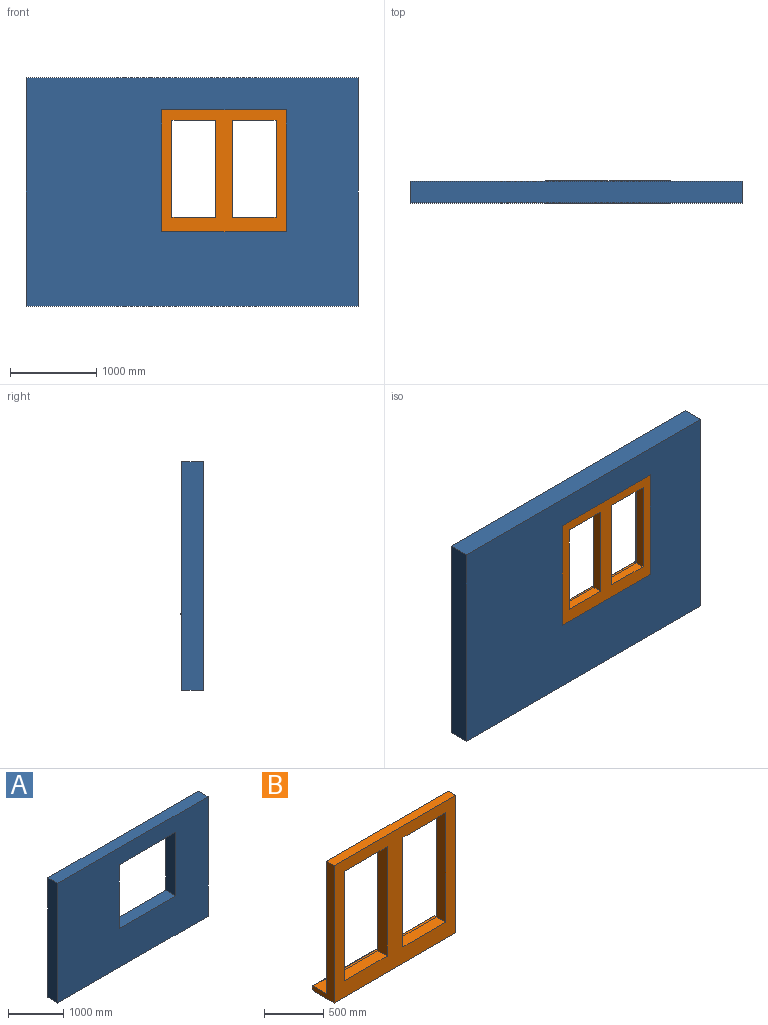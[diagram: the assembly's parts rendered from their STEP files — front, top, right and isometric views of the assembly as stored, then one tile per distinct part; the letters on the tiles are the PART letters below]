
ASSEMBLY  parts=2 mates=1
PART A: 10 faces, bbox 3860x250x2655 mm
  f0: plane 3860x250mm, normal (0,0,1), area 965000mm2, adj f1,f3,f4,f5
  f1: plane 2655x250mm, normal (-1,0,0), area 663750mm2, adj f0,f2,f3,f5
  f2: plane 3860x250mm, normal (0,0,-1), area 965000mm2, adj f1,f3,f4,f5
  f3: plane 3860x2655mm, normal (0,-1,0), area 8193648.2mm2, adj f0,f1,f2,f4,f6,f7,f8,f9
  f4: plane 2655x250mm, normal (1,0,0), area 663750mm2, adj f0,f2,f3,f5
  f5: plane 3860x2655mm, normal (0,1,0), area 8193648.2mm2, adj f0,f1,f2,f4,f6,f7,f8,f9
  f6: plane 1417x250mm, normal (1,0,0), area 354250.3mm2, adj f3,f5,f7,f9
  f7: plane 1450x250mm, normal (0,0,-1), area 362500mm2, adj f3,f5,f6,f8
  f8: plane 1417x250mm, normal (-1,0,0), area 354250.3mm2, adj f3,f5,f7,f9
  f9: plane 1450x250mm, normal (0,0,1), area 362500mm2, adj f3,f5,f6,f8
PART B: 29 faces, bbox 1450x263x1417 mm
  f0: plane 1450x1417mm, normal (0,-1,0), area 901835.8mm2, adj f16,f17,f18,f19,f20,f21,f22,f23
  f1: plane 1450x12mm, normal (0,1,0), area 17401.8mm2, adj f24,f25,f26,f28
  f2: plane 671x20mm, normal (0,0,-1), area 13420mm2, adj f3,f5,f10,f12
  f3: plane 1288x20mm, normal (-1,0,0), area 25760mm2, adj f2,f4,f10,f12
  f4: plane 671x20mm, normal (0,0,1), area 13420mm2, adj f3,f5,f10,f12
  f5: plane 1288x20mm, normal (1,0,0), area 25760mm2, adj f2,f4,f10,f12
  f6: plane 1288x20mm, normal (-1,0,0), area 25760mm2, adj f7,f9,f11,f12
  f7: plane 671x20mm, normal (0,0,1), area 13420mm2, adj f6,f8,f11,f12
  f8: plane 1288x20mm, normal (1,0,0), area 25760mm2, adj f7,f9,f11,f12
  f9: plane 671x20mm, normal (0,0,-1), area 13420mm2, adj f6,f8,f11,f12
  f10: plane 1288x671mm, normal (0,1,0), area 287840mm2, adj f2,f3,f4,f5,f16,f17,f18,f19
  f11: plane 1288x671mm, normal (0,1,0), area 287840mm2, adj f6,f7,f8,f9,f20,f21,f22,f23
  f12: plane 1450x1368mm, normal (0,1,0), area 255104mm2, adj f2,f3,f4,f5,f6,f7,f8,f9
  f13: cylinder r=6mm len=1450mm, axis (1,0,0), area 12497.3mm2, adj f14,f15,f24,f26
  f14: plane 1450x31.8mm, normal (0,0.99,0.13), area 46534.2mm2, adj f13,f24,f25,f26
  f15: plane 1450x162.76mm, normal (0,0,1), area 235996.6mm2, adj f12,f13,f24,f26
  f16: plane 1128x110mm, normal (1,0,0), area 124080mm2, adj f0,f10,f17,f19
  f17: plane 511x110mm, normal (0,0,-1), area 56210mm2, adj f0,f10,f16,f18
  f18: plane 1128x110mm, normal (-1,0,0), area 124080mm2, adj f0,f10,f17,f19
  f19: plane 511x110mm, normal (0,0,1), area 56210mm2, adj f0,f10,f16,f18
  f20: plane 1128x110mm, normal (1,0,0), area 124080mm2, adj f0,f11,f21,f23
  f21: plane 511x110mm, normal (0,0,-1), area 56210mm2, adj f0,f11,f20,f22
  f22: plane 1128x110mm, normal (-1,0,0), area 124080mm2, adj f0,f11,f21,f23
  f23: plane 511x110mm, normal (0,0,1), area 56210mm2, adj f0,f11,f20,f22
  f24: plane 1417x263mm, normal (-1,0,0), area 135753.1mm2, adj f0,f1,f12,f13,f14,f15,f25,f27
  f25: plane 1450x13mm, normal (0,0,-1), area 18850mm2, adj f1,f14,f24,f26
  f26: plane 1417x263mm, normal (1,0,0), area 135754.5mm2, adj f0,f1,f12,f13,f14,f15,f25,f27
  f27: plane 1450x90mm, normal (0,0,1), area 130500mm2, adj f0,f12,f24,f26
  f28: plane 1450x250mm, normal (0,0,-1), area 362500mm2, adj f0,f1,f24,f26
PLACE A t=(-1792.59,-2013.66,31.72)mm fixed
PLACE B t=(-1792.59,-2013.66,31.72)mm
MATE fastened B.f28 <-> A.f9  axis (0,0,-1) through (509.41,-2138.66,896.72)mm
